FCSTD DOCUMENT  (FreeCAD 0.19R24276 (Git))
Label: Master_sketch
License: All rights reserved
LicenseURL: http://en.wikipedia.org/wiki/All_rights_reserved
objects: Sketcher::SketchObject×1, PartDesign::Body×1
note: 2 computed .brp shape members not serialized (recipe doc carries the construction recipe); baked Part::Feature solids carry a one-line shape summary decoded from their .brp

FEATURE [Sketcher::SketchObject] Sketch
  FullyConstrained = false
  MapMode = 5
  Support = -> [XY_Plane]
  sketch-geometry (3):
    g0: LineSegment StartX=0 StartY=92 StartZ=0 EndX=-26.3719 EndY=55.5374 EndZ=0
    g1: Circle CenterX=0 CenterY=13.0577 CenterZ=0 NormalX=0 NormalY=0 NormalZ=1 AngleXU=0 Radius=8
    g2: LineSegment StartX=0 StartY=13.0577 StartZ=0 EndX=-26.3719 EndY=55.5374 EndZ=0
  constraints (8):
    c: PointOnObject(g0,g-2)
    c: Distance(g0) = 45
    c: PointOnObject(g1,g-2)
    c: Coincident(g2,g1)
    c: Coincident(g2,g0)
    c: Diameter(g1) = 16
    c: DistanceY(g-1,g0) = 92
    c: Distance(g2) = 50
FEATURE [PartDesign::Body] Body
  Group = -> [Sketch]
  Origin = -> Origin
